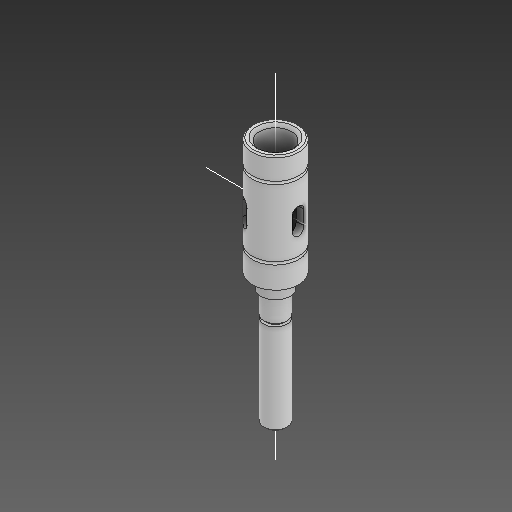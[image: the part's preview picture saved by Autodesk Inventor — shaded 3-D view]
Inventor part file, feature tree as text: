
AUTODESK INVENTOR PART (.ipt)
format: ipt  version: 2021 (Build 250183000, 183)  size: 216,576 bytes
history: native  units: in
note: dims shown in document units (in); Inventor stores cm internally (conversion verified against a paired STEP export)
features: sketch x9, other x8, plane x3
ambient origin geometry x8: Origin, YZ Plane, XZ Plane, XY Plane, X Axis, Y Axis, Z Axis, Center Point
bodies: Solid1 (feature_tree)
feature tree (20):
  other  "iner_sleeve.ipt"
  other  "Solid1::iner_sleeve.ipt"
  other  "TaggingFeature1"
  sketch  "Sketch1"  dims[d0=0.3937in]
  sketch  "Sketch2"
  sketch  "Sketch3"
  sketch  "Sketch5"
  sketch  "Sketch6"
  sketch  "Sketch7"
  sketch  "Sketch8"
  sketch  "Sketch10"
  sketch  "Sketch11"
  plane  "Work Plane1"
  plane  "Work Plane2"
  plane  "Work Plane3"
  other  "Work Axis1"
  other  "Work Axis2"
  other  "Work Axis3"
  other  "Srf1"
  other  "Srf1::Derived"
